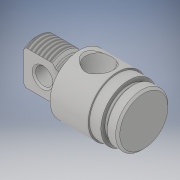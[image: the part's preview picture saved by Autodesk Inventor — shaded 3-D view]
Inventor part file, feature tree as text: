
AUTODESK INVENTOR PART (.ipt)
format: ipt  version: 2019 (Build 230136000, 136)  size: 280,064 bytes
history: native  units: mm
features: other x126, sketch x7, revolve x6, thread x1, extrude x1
ambient origin geometry x8: Origin, YZ Plane, XZ Plane, XY Plane, X Axis, Y Axis, Z Axis, Center Point
bodies: Solid1 (feature_tree)
feature tree (141):
  revolve  "Revolution1"  Angle=360.0deg
  revolve  "Revolution2"  Angle=360.0deg
  thread  "Thread1"  [1 undecoded]
  revolve  "Revolution3"  [1 undecoded]
  revolve  "Revolution4"  [1 undecoded]
  revolve  "Revolution5"  [1 undecoded]
  extrude  "Extrusion1"  [1 undecoded]
  revolve  "Revolution6"  [1 undecoded]
  other  "b1_XY"
  other  "b1_YZ"
  other  "b1_ZX"
  other  "b1_X"
  other  "b1_Y"
  other  "b1_Z"
  other  "b1_Center"
  other  "b2_XY"
  other  "b2_YZ"
  other  "b2_ZX"
  other  "b2_X"
  other  "b2_Y"
  other  "b2_Z"
  other  "b2_Center"
  other  "cl1_XY"
  other  "cl1_YZ"
  other  "cl1_ZX"
  other  "cl1_X"
  other  "cl1_Y"
  other  "cl1_Z"
  other  "cl1_Center"
  other  "cl2_XY"
  other  "cl2_YZ"
  other  "cl2_ZX"
  other  "cl2_X"
  other  "cl2_Y"
  other  "cl2_Z"
  other  "cl2_Center"
  other  "ecut1_XY"
  other  "ecut1_YZ"
  other  "ecut1_ZX"
  other  "ecut1_X"
  other  "ecut1_Y"
  other  "ecut1_Z"
  other  "ecut1_Center"
  other  "ecut2_XY"
  other  "ecut2_YZ"
  other  "ecut2_ZX"
  other  "ecut2_X"
  other  "ecut2_Y"
  other  "ecut2_Z"
  other  "ecut2_Center"
  other  "ee_XY"
  other  "ee_YZ"
  other  "ee_ZX"
  other  "ee_X"
  other  "ee_Y"
  other  "ee_Z"
  other  "ee_Center"
  other  "od1_XY"
  other  "od1_YZ"
  other  "od1_ZX"
  other  "od1_X"
  other  "od1_Y"
  other  "od1_Z"
  other  "od1_Center"
  other  "od2_XY"
  other  "od2_YZ"
  other  "od2_ZX"
  other  "od2_X"
  other  "od2_Y"
  other  "od2_Z"
  other  "od2_Center"
  other  "od3_XY"
  other  "od3_YZ"
  other  "od3_ZX"
  other  "od3_X"
  other  "od3_Y"
  other  "od3_Z"
  other  "od3_Center"
  other  "od4_XY"
  other  "od4_YZ"
  other  "od4_ZX"
  other  "od4_X"
  other  "od4_Y"
  other  "od4_Z"
  other  "od4_Center"
  other  "to_body_XY"
  other  "to_body_YZ"
  other  "to_body_ZX"
  other  "to_body_X"
  other  "to_body_Y"
  other  "to_body_Z"
  other  "to_body_Center"
  other  "to_dummy_XY"
  other  "to_dummy_YZ"
  other  "to_dummy_ZX"
  other  "to_dummy_X"
  other  "to_dummy_Y"
  other  "to_dummy_Z"
  other  "to_dummy_Center"
  other  "to_nut_XY"
  other  "to_nut_YZ"
  other  "to_nut_ZX"
  other  "to_nut_X"
  other  "to_nut_Y"
  other  "to_nut_Z"
  other  "to_nut_Center"
  other  "to_pin_XY"
  other  "to_pin_YZ"
  other  "to_pin_ZX"
  other  "to_pin_X"
  other  "to_pin_Y"
  other  "to_pin_Z"
  other  "to_pin_Center"
  other  "to_stroke_adjuster_XY"
  other  "to_stroke_adjuster_YZ"
  other  "to_stroke_adjuster_ZX"
  other  "to_stroke_adjuster_X"
  other  "to_stroke_adjuster_Y"
  other  "to_stroke_adjuster_Z"
  other  "to_stroke_adjuster_Center"
  other  "z1_XY"
  other  "z1_YZ"
  other  "z1_ZX"
  other  "z1_X"
  other  "z1_Y"
  other  "z1_Z"
  other  "z1_Center"
  other  "z2_XY"
  other  "z2_YZ"
  other  "z2_ZX"
  other  "z2_X"
  other  "z2_Y"
  other  "z2_Z"
  other  "z2_Center"
  sketch  "Sketch_1"  dims[d0=360.0deg d1=360.0deg]
  sketch  "Sketch_2"  dims[d2=9.87933mm d3=0.0mm d4=360.0deg d5=360.0deg]
  sketch  "Sketch_6"  dims[d6=360.0deg d7=15.9766mm d8=0.0mm]
  sketch  "Sketch_8"  dims[d9=360.0deg]
  sketch  "Sketch_29"  dims[d10=0.0mm d11=0.0mm d12=0.0mm d13=0.0mm d14=0.0mm d15=0.0mm d16=0.0mm d17=0.0mm d18=0.0mm d19=0.0mm d20=0.0mm d21=0.0mm]
  sketch  "Sketch_38"
  sketch  "Sketch_36"
note: 6 required parameter values undecoded (feature->parameter linkage not recoverable at this tier; creation-order binding heuristic only, values carry confidence <= 0.55)